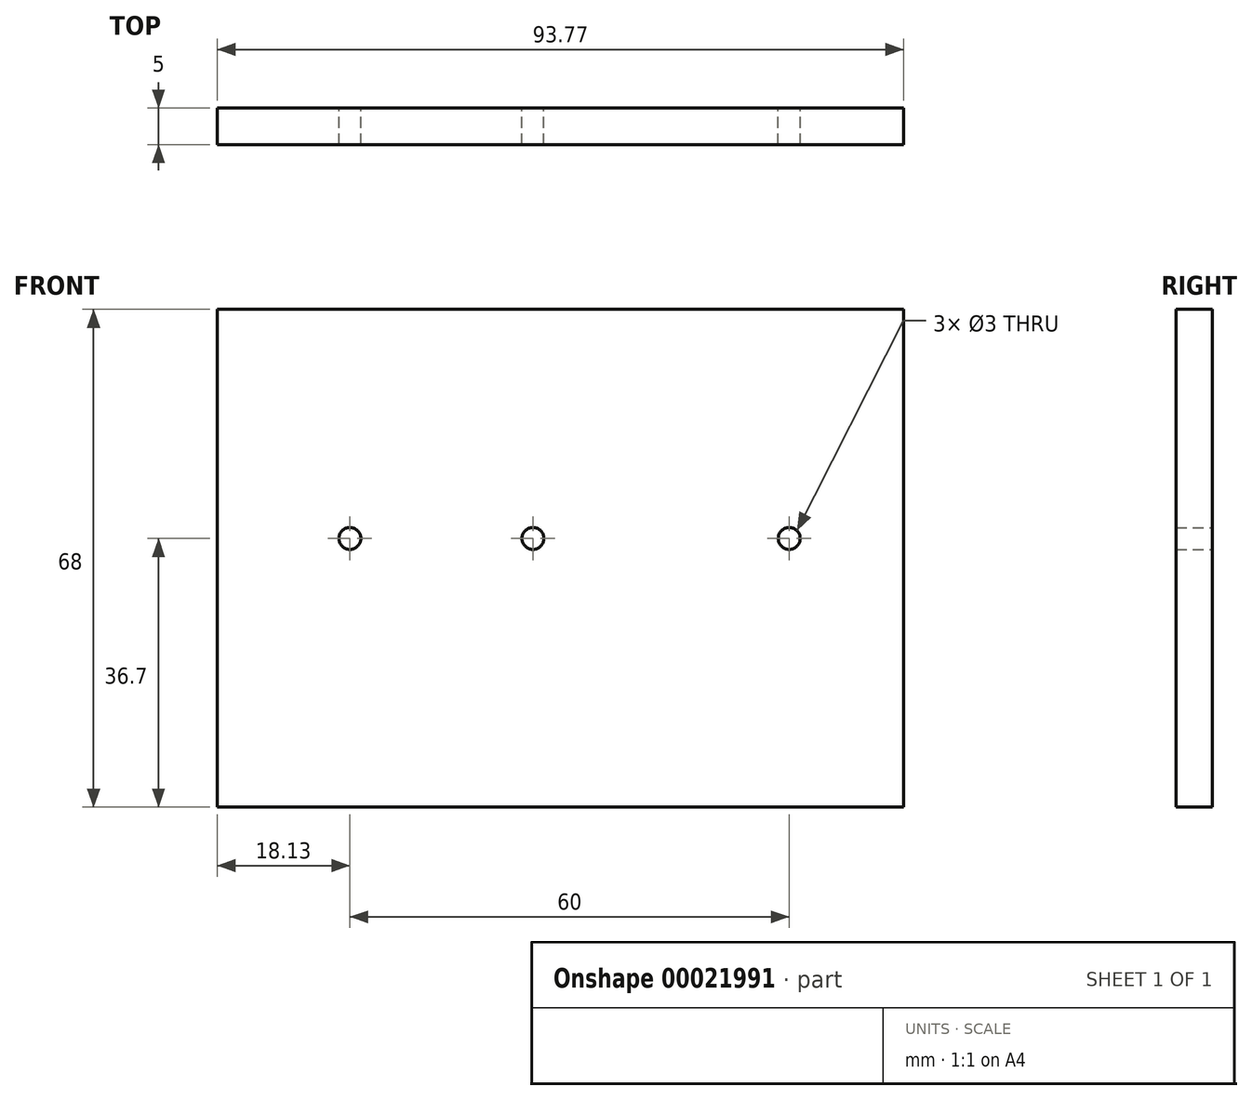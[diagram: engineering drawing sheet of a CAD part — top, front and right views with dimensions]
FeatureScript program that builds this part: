
annotation { "Feature Type Name" : "Feature", "Feature Type Description" : "" }
export const myFeature = defineFeature(function(context is Context, id is Id, definition is map)
    precondition{}
    {
        {
            var Q0;
            Q0=qCreatedBy(makeId("Front.planeOp"),FACE);
            var sketch = newSketch(context, id + "F0", { "sketchPlane" : qUnion([Q0])});
            skLineSegment(sketch, "E0.bottom", {"start": v(-43.13, 31.3) * mm, "end": v(50.64, 31.3) * mm});
            skLineSegment(sketch, "E0.top", {"start": v(-43.13, -36.7) * mm, "end": v(50.64, -36.7) * mm});
            skLineSegment(sketch, "E0.left", {"start": v(-43.13, 31.3) * mm, "end": v(-43.13, -36.7) * mm});
            skLineSegment(sketch, "E0.right", {"start": v(50.64, 31.3) * mm, "end": v(50.64, -36.7) * mm});
            skCircle(sketch, "E1", {"center": v(35, 0) * mm, "radius": 1.5 * mm});
            skCircle(sketch, "E2", {"center": v(0, 0) * mm, "radius": 1.5 * mm});
            skCircle(sketch, "E3", {"center": v(-25, 0) * mm, "radius": 1.5 * mm});
            skSolve(sketch);
        }
        {
            var Q0;
            Q0=makeQuery(id+"F0.imprint","IMPRINT",FACE,{"disambiguationData":[TD([[makeQuery(id+"F0.imprint","IMPRINT",EDGE,{"derivedFrom":sQuery(id+"F0.wireOp",EDGE,"E0.bottom")}),-1.0]])]});
            extrude(context, id + "F1", {"entities" : qUnion([Q0]), "depth" : 5 * mm});
        }
    });
